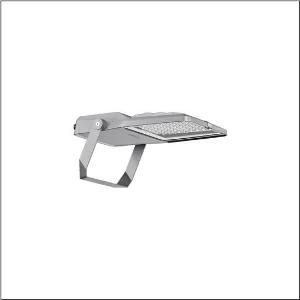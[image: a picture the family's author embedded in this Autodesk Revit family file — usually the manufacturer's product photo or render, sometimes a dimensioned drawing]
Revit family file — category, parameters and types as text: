
# Revit family: floodlight_fl_21_iq_mini___pl52_5xa7772b4d1a_9164
name_source: partatom
category: Lighting Fixtures
units: mm (PartAtom-declared; Revit-internal decimal feet)

## family parameters
Cut with Voids When Loaded = No
Host = Face
Light Source = No
Part Type = Normal
Room Calculation Point = No
Round Connector Dimension = Use Diameter
Shared = No

## types (1)
- --- (1 x LED, 6490 lm, 45.5 W, 4000K)
    Apparent Load = 46 VA
    CIE Flux Codes = 26 60 98 100 100
    Color Rendering = 70
    Color Temperature = 4000K
    Default Elevation = 1800 mm
    Description = Floodlight FL 21 iQ mini, floodlight, primary light control with lens, of PMMA, primary optical cover: protective disc, of toughened safety glass, transparent, light distribution: PL52, light emission: direct distribution, installation type: surface-mounted, LED, High Power LED, rated luminous flux: 6.490lm, luminous efficacy: 143lm/W, light colour: 740, colour temperature: 4000K, control: Street-Remote, Auto-Match, Temp-Guard, Night-Set, Smart-Wire, Desk-Remote (wireless, voltage-free reading and setting of iQ features in the workshop via application-optimized NFC function/RFID function), optimised constant luminous flux control (CLO 2.0), with terminal, 6-pole, mains connection: 220..240V, AC, 50/60Hz, start of lifetime: 46W, end of service life: 48W, reduction: 22W, luminaire housing, of diecast aluminium, powder-coated, Siteco® metallic grey (DB 702S), corrosivity category C5 mid according to DIN EN ISO 12944, sealing non-destructively replaceable, mounting bracket, of steel, galvanised, powder-coated, Siteco® metallic grey (DB 702S), protection rating (complete): IP66, insulation class (complete): insulation class II (safety insulation), certification: CE, ENEC, VDE, protection symbol: D, impact resistance: IK08, permissible operating ambient temperature: -40..+40°C, permissible operating ambient temperature for outdoor applications: -40..+50°C, standard: DIN EN 12944, LABS conformity tested according to VDMA 24364:2018-05, packaging unit: 1 piece

Light Distribution: PL52
    Height = 70 mm
    Lamp = 1 x LED
    Lamp Light Flux = 6490 lm
    Lamp Power = 45.5 W
    Lamp count = 1
    Length = 485 mm
    Luminous efficacy = 143 lm/W
    Manufacturer = Siteco
    ModVariant = No
    Model = 5XA7772B4D1A
    Number of Poles = 1
    OnlyDefault = Yes
    Power Factor = 1
    Product Name = Floodlight FL 21 iQ mini | PL52
    Product group = floodlight | pylon annexe
    ProductGroupID = 6200
    Protection Class = Protection class II
    Protection Degree = IP 66
    RLX_Detail_Level = 1
    RLX_Emergency_Light_Flux = 0 lm
    RLX_Emergency_Type = 0
    RLX_Emergency_Type_DB = No
    RlxData = <blob elided: 96381 chars, md5=84f4abf5>
    Socket = socket
    Standby Power = 0 W
    System Light Flux = 6490 lm
    System Power = 46 W
    Type Comments = factory setting: luminous flux: 100 % | dim-lin: 254 | 463 mA
    Type Image = l_1006845.jpg
    URL = http://relux.com
    VarID = @adj_097071
    Voltage = 0 V
    Weight = 0.00 kg
    Width = 337 mm

## geometry (parser evidence)
native form markers: Blend x4, Sweep x10
no freeform markers — native parametric forms only
